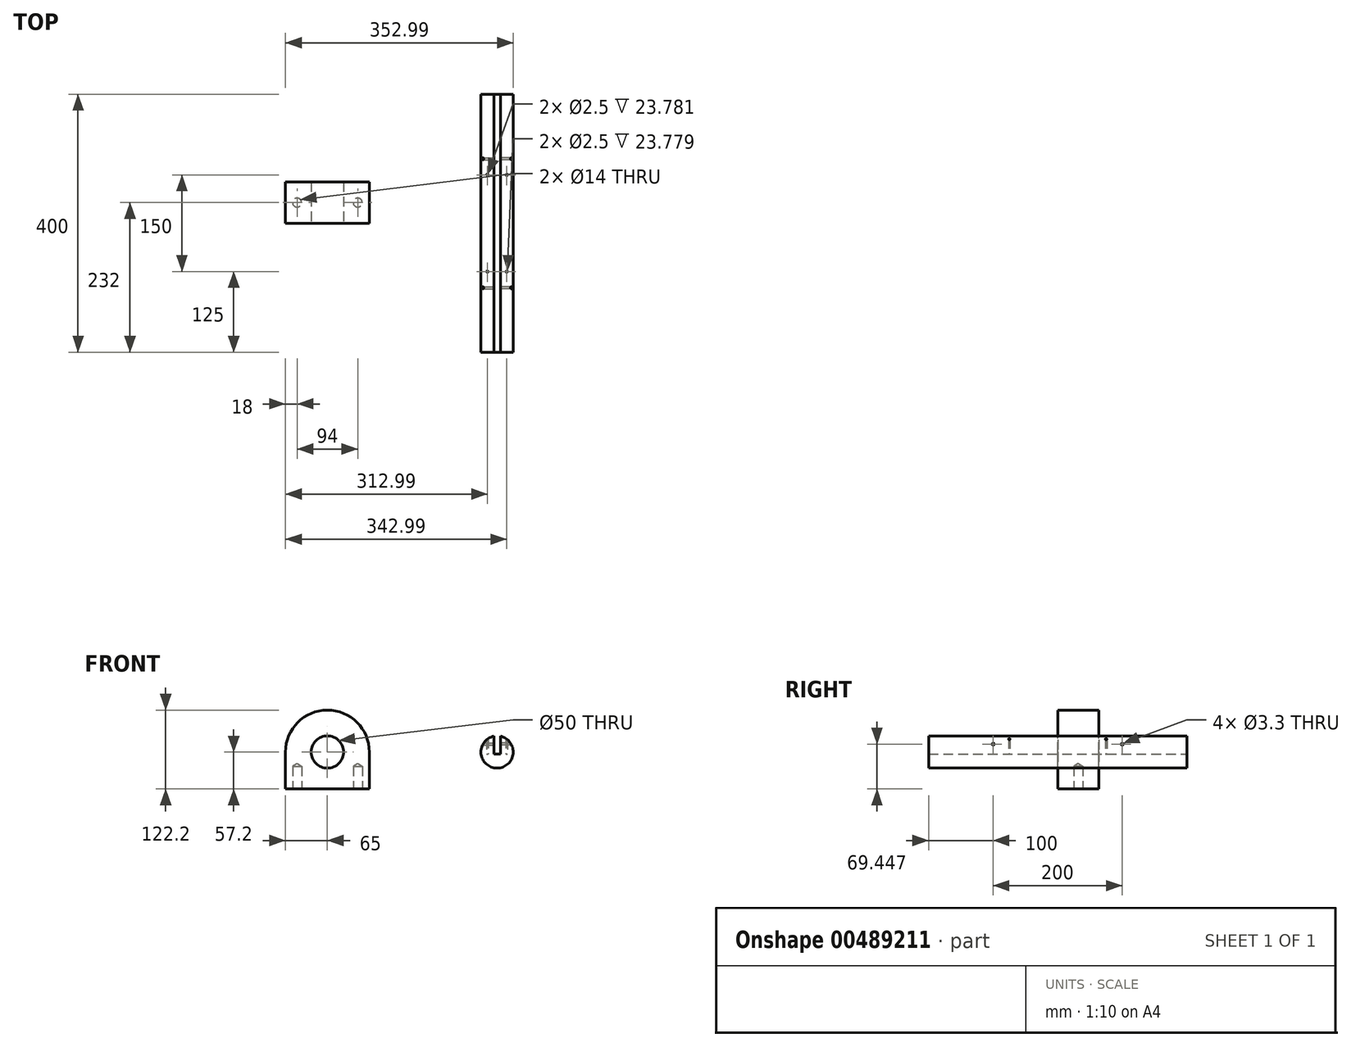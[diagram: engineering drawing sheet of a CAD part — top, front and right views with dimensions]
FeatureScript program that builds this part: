
annotation { "Feature Type Name" : "Feature", "Feature Type Description" : "" }
export const myFeature = defineFeature(function(context is Context, id is Id, definition is map)
    precondition{}
    {
        {
            var Q0;
            Q0=qCreatedBy(makeId("Front.planeOp"),FACE);
            var sketch = newSketch(context, id + "F0", { "sketchPlane" : qUnion([Q0])});
            skCircle(sketch, "E0", {"center": v(0, 0) * mm, "radius": 25 * mm});
            skArc(sketch, "E1", {"start": v(65, 0) * mm, "mid": v(0, 65) * mm, "end": v(-65, 0) * mm});
            skLineSegment(sketch, "E2.top", {"start": v(0, -57.2) * mm, "end": v(65, -57.2) * mm});
            skLineSegment(sketch, "E2.right", {"start": v(65, 0) * mm, "end": v(65, -57.2) * mm});
            skLineSegment(sketch, "E3.bottom", {"start": v(0, -57.2) * mm, "end": v(-65, -57.2) * mm});
            skLineSegment(sketch, "E3.right", {"start": v(-65, -57.2) * mm, "end": v(-65, 0) * mm});
            skSolve(sketch);
        }
        {
            var Q0;
            Q0=makeQuery(id+"F0.imprint","IMPRINT",FACE,{"disambiguationData":[TD([[makeQuery(id+"F0.imprint","IMPRINT",EDGE,{"derivedFrom":sQuery(id+"F0.wireOp",EDGE,"E0")}),-1.0]])]});
            var Q1;
            Q1=makeQuery(id+"F0.imprint","IMPRINT",FACE,{"disambiguationData":[TD([[makeQuery(id+"F0.imprint","IMPRINT",EDGE,{"derivedFrom":sQuery(id+"F0.wireOp",EDGE,"xSiT5YzH-nQam-14kf-8dS3-OH7JncKjmuEs.bottom")}),-1.0]])]});
            var Q2;
            Q2=makeQuery(id+"F0.imprint","IMPRINT",FACE,{"disambiguationData":[TD([[makeQuery(id+"F0.imprint","IMPRINT",EDGE,{"derivedFrom":sQuery(id+"F0.wireOp",EDGE,"nXCXNCpR-T3J8-dAdy-RV02-bPo7PzRIS1eH.bottom")}),1.0]])]});
            extrude(context, id + "F1", {"entities" : qUnion([Q0, Q1, Q2]), "oppositeDirection" : true, "depth" : 64 * mm, "offsetDistance" : 25 * mm});
        }
        {
            var Q0;
            Q0=qCreatedBy(makeId("Front.planeOp"),FACE);
            var sketch = newSketch(context, id + "F2", { "sketchPlane" : qUnion([Q0])});
            skArc(sketch, "E4", {"start": v(287.99, 0.1) * mm, "mid": v(282.32, 15.85) * mm, "end": v(267.99, 24.5) * mm});
            skLineSegment(sketch, "E5", {"start": v(247.99, 0) * mm, "end": v(257.99, 0) * mm, "construction": true});
            skLineSegment(sketch, "E6.right", {"start": v(267.99, -2.9) * mm, "end": v(267.99, 24.5) * mm});
            skLineSegment(sketch, "E7.right", {"start": v(257.99, -2.9) * mm, "end": v(257.99, 24.5) * mm});
            skArc(sketch, "E8.trimOffspring", {"start": v(237.99, 0) * mm, "mid": v(263.04, -25) * mm, "end": v(287.99, 0.1) * mm});
            skPoint(sketch, "E9.orphan", {"position": v(287.99, 0.1) * mm});
            skPoint(sketch, "E6.bottom.end.orphan", {"position": v(267.99, 0.1) * mm});
            skPoint(sketch, "E10.end.orphan", {"position": v(262.99, 25) * mm});
            skArc(sketch, "E11.trimOffspring", {"start": v(257.99, 24.5) * mm, "mid": v(243.62, 15.81) * mm, "end": v(237.99, 0) * mm});
            skPoint(sketch, "E12.orphan", {"position": v(257.99, 25) * mm});
            skPoint(sketch, "E13.orphan", {"position": v(267.99, 25) * mm});
            skLineSegment(sketch, "E14.trimOffspring", {"start": v(257.99, -2.9) * mm, "end": v(267.99, -2.9) * mm});
            skSolve(sketch);
        }
        {
            var Q0;
            Q0 = qSketchRegion(id + "F2", true);
            extrude(context, id + "F3", {"entities" : qUnion([Q0]), "endBound" : BoundingType.SYMMETRIC, "depth" : 400 * mm, "offsetDistance" : 25 * mm});
        }
        {
            var Q0;
            Q0=makeQuery(id+"F3.opExtrude","SWEPT_FACE",FACE,{"disambiguationData":[OSD([sQuery(id+"F2.wireOp",EDGE,"E7.right")])]});
            var sketch = newSketch(context, id + "F4", { "sketchPlane" : qUnion([Q0])});
            skLineSegment(sketch, "E15", {"start": v(0, 0) * mm, "end": v(0, 24.5) * mm});
            skPoint(sketch, "E16", {"position": v(100, 12.25) * mm});
            skPoint(sketch, "E17", {"position": v(-100, 12.25) * mm});
            skSolve(sketch);
        }
        {
            var Q0;
            Q0=makeQuery(id+"F3.opExtrude","SWEPT_FACE",FACE,{"disambiguationData":[OSD([sQuery(id+"F2.wireOp",EDGE,"E6.right")])]});
            var sketch = newSketch(context, id + "F5", { "sketchPlane" : qUnion([Q0])});
            skLineSegment(sketch, "E18", {"start": v(0, 0) * mm, "end": v(0, 24.5) * mm});
            skPoint(sketch, "E19", {"position": v(-100, 12.25) * mm});
            skPoint(sketch, "E20", {"position": v(100, 12.25) * mm});
            skSolve(sketch);
        }
        {
            var Q0;
            Q0=sQuery(id+"F4.wireOp",VERTEX,"E16");
            var Q1;
            Q1=sQuery(id+"F5.wireOp",VERTEX,"E19");
            var Q2;
            Q2=sQuery(id+"F4.wireOp",VERTEX,"E17");
            var Q3;
            Q3=sQuery(id+"F5.wireOp",VERTEX,"E20");
            var Q4;
            Q4=makeQuery(id+"F3.opExtrude","SWEPT_BODY",BODY,{"disambiguationData":[OSD([sQuery(id+"F2.wireOp",EDGE,"E4"),sQuery(id+"F2.wireOp",EDGE,"E6.right"),sQuery(id+"F2.wireOp",EDGE,"E7.right"),sQuery(id+"F2.wireOp",EDGE,"E8.trimOffspring"),sQuery(id+"F2.wireOp",EDGE,"E11.trimOffspring"),sQuery(id+"F2.wireOp",EDGE,"E14.trimOffspring")])]});
            hole(context, id + "F6", {"style" : HoleStyle.SIMPLE, "endStyle" : HoleEndStyle.THROUGH, "standardTappedOrClearance" : lookupTablePath({ "standard" : "ISO", "engagement" : "75%", "pitch" : "0.7 mm", "size" : "M4", "type" : "Tapped" }), "standardBlindInLast" : lookupTablePath({ "standard" : "ISO", "fit" : "Normal", "engagement" : "75%", "pitch" : "0.7 mm", "size" : "M4", "type" : "Clearance & tapped" }), "holeDiameter" : 3.3 * mm, "majorDiameter" : 4 * mm, "showTappedDepth" : true, "isTappedThrough" : true, "tappedDepth" : 12 * mm, "tapClearance" : 3, "startFromSketch" : true, "locations" : qUnion([Q0, Q1, Q2, Q3]), "scope" : qUnion([Q4])});
        }
        {
            var Q0;
            Q0=makeQuery(id+"F3.opExtrude","SWEPT_FACE",FACE,{"disambiguationData":[OSD([sQuery(id+"F2.wireOp",EDGE,"E14.trimOffspring")])]});
            var sketch = newSketch(context, id + "F7", { "sketchPlane" : qUnion([Q0])});
            skLineSegment(sketch, "E21", {"start": v(257.99, 0) * mm, "end": v(237.99, 0) * mm});
            skPoint(sketch, "E22", {"position": v(247.99, 75) * mm});
            skPoint(sketch, "E22.positionSnap0", {"position": v(247.99, 0) * mm});
            skPoint(sketch, "E23", {"position": v(247.99, -75) * mm});
            skPoint(sketch, "E24.1.0.0", {"position": v(277.99, -75) * mm});
            skPoint(sketch, "E24.1.0.1", {"position": v(277.99, 75) * mm});
            skLineSegment(sketch, "E24.direction1", {"start": v(247.99, -75) * mm, "end": v(277.99, -75) * mm, "construction": true});
            skSolve(sketch);
        }
        {
            var Q0;
            Q0=sQuery(id+"F7.wireOp",VERTEX,"E23");
            var Q1;
            Q1=sQuery(id+"F7.wireOp",VERTEX,"E24.1.0.0");
            var Q2;
            Q2=sQuery(id+"F7.wireOp",VERTEX,"E24.1.0.1");
            var Q3;
            Q3=sQuery(id+"F7.wireOp",VERTEX,"E22");
            var Q4;
            Q4=makeQuery(id+"F3.opExtrude","SWEPT_BODY",BODY,{"disambiguationData":[OSD([sQuery(id+"F2.wireOp",EDGE,"E4"),sQuery(id+"F2.wireOp",EDGE,"E6.right"),sQuery(id+"F2.wireOp",EDGE,"E7.right"),sQuery(id+"F2.wireOp",EDGE,"E8.trimOffspring"),sQuery(id+"F2.wireOp",EDGE,"E11.trimOffspring"),sQuery(id+"F2.wireOp",EDGE,"E14.trimOffspring")])]});
            hole(context, id + "F8", {"style" : HoleStyle.SIMPLE, "endStyle" : HoleEndStyle.BLIND, "oppositeDirection" : true, "standardTappedOrClearance" : lookupTablePath({ "standard" : "ISO", "engagement" : "75%", "pitch" : "0.5 mm", "size" : "M3", "type" : "Tapped" }), "standardBlindInLast" : lookupTablePath({ "standard" : "ISO", "fit" : "Normal", "engagement" : "75%", "pitch" : "0.5 mm", "size" : "M3", "type" : "Clearance & tapped" }), "holeDiameter" : 2.5 * mm, "majorDiameter" : 3 * mm, "showTappedDepth" : true, "holeDepth" : 25 * mm, "isTappedThrough" : true, "tappedDepth" : 23.5 * mm, "tapClearance" : 3, "startFromSketch" : true, "locations" : qUnion([Q0, Q1, Q2, Q3]), "scope" : qUnion([Q4])});
        }
        {
            var Q0;
            Q0=makeQuery(id+"F1.opExtrude","SWEPT_FACE",FACE,{"disambiguationData":[OSD([sQuery(id+"F0.wireOp",EDGE,"E2.top"),sQuery(id+"F0.wireOp",EDGE,"E3.bottom")])]});
            var sketch = newSketch(context, id + "F9", { "sketchPlane" : qUnion([Q0])});
            skLineSegment(sketch, "E25", {"start": v(0, 0) * mm, "end": v(0, -64) * mm});
            skPoint(sketch, "E26", {"position": v(47, -32) * mm});
            skPoint(sketch, "E26.positionSnap0", {"position": v(0, -32) * mm});
            skPoint(sketch, "E27", {"position": v(-47, -32) * mm});
            skSolve(sketch);
        }
        {
            var Q0;
            Q0=sQuery(id+"F9.wireOp",VERTEX,"E27");
            var Q1;
            Q1=sQuery(id+"F9.wireOp",VERTEX,"E26");
            var Q2;
            Q2=makeQuery(id+"F1.opExtrude","SWEPT_BODY",BODY,{"disambiguationData":[OSD([sQuery(id+"F0.wireOp",EDGE,"E0"),sQuery(id+"F0.wireOp",EDGE,"E1"),sQuery(id+"F0.wireOp",EDGE,"ypRxsnW0-4U5n-uhFx-UJqm-rLp9NCDRqHTf.top"),sQuery(id+"F0.wireOp",EDGE,"ypRxsnW0-4U5n-uhFx-UJqm-rLp9NCDRqHTf.left"),sQuery(id+"F0.wireOp",EDGE,"LrQsNWpV-xNCb-v41C-x7TN-4qpLN4L3xsnU.top"),sQuery(id+"F0.wireOp",EDGE,"LrQsNWpV-xNCb-v41C-x7TN-4qpLN4L3xsnU.left"),sQuery(id+"F0.wireOp",EDGE,"xSiT5YzH-nQam-14kf-8dS3-OH7JncKjmuEs.left"),sQuery(id+"F0.wireOp",EDGE,"nXCXNCpR-T3J8-dAdy-RV02-bPo7PzRIS1eH.left")])]});
            hole(context, id + "F10", {"style" : HoleStyle.SIMPLE, "endStyle" : HoleEndStyle.BLIND, "standardTappedOrClearance" : lookupTablePath({ "standard" : "ISO", "engagement" : "75%", "pitch" : "2 mm", "size" : "M16", "type" : "Tapped" }), "standardBlindInLast" : lookupTablePath({ "standard" : "ISO", "fit" : "Normal", "engagement" : "75%", "pitch" : "2 mm", "size" : "M16", "type" : "Clearance & tapped" }), "holeDiameter" : 14 * mm, "majorDiameter" : 16 * mm, "showTappedDepth" : true, "holeDepth" : 35 * mm, "isTappedThrough" : true, "tappedDepth" : 25 * mm, "tapClearance" : 5, "startFromSketch" : true, "locations" : qUnion([Q0, Q1]), "scope" : qUnion([Q2])});
        }
    });
